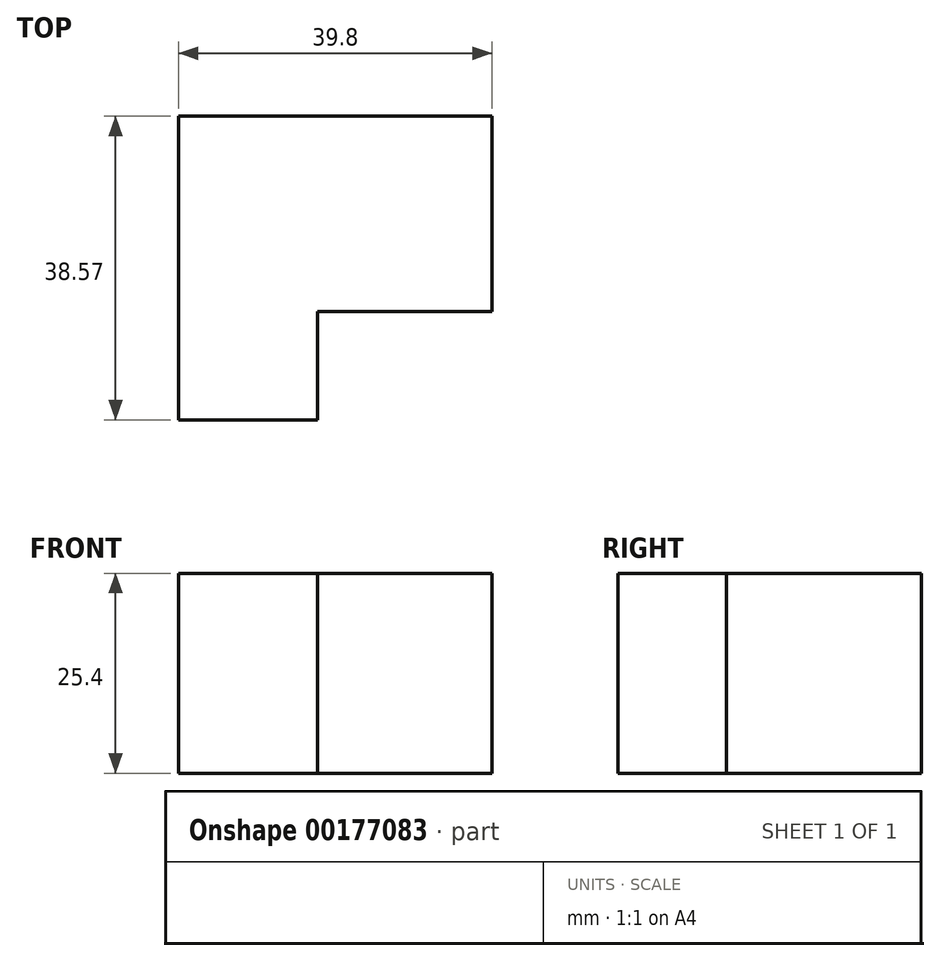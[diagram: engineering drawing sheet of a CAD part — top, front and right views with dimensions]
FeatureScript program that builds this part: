
annotation { "Feature Type Name" : "Feature", "Feature Type Description" : "" }
export const myFeature = defineFeature(function(context is Context, id is Id, definition is map)
    precondition{}
    {
        {
            var Q0;
            Q0=qCreatedBy(makeId("Top.planeOp"),FACE);
            var sketch = newSketch(context, id + "F0", { "sketchPlane" : qUnion([Q0])});
            skLineSegment(sketch, "E0.bottom", {"start": v(0, 0) * mm, "end": v(17.65, 0) * mm});
            skLineSegment(sketch, "E0.top", {"start": v(0, 24.33) * mm, "end": v(17.65, 24.33) * mm});
            skLineSegment(sketch, "E0.left", {"start": v(0, 0) * mm, "end": v(0, 24.33) * mm});
            skLineSegment(sketch, "E0.right", {"start": v(17.65, 0) * mm, "end": v(17.65, 24.33) * mm});
            skLineSegment(sketch, "E1.bottom", {"start": v(17.65, 24.33) * mm, "end": v(39.8, 24.33) * mm});
            skLineSegment(sketch, "E1.top", {"start": v(17.65, 13.77) * mm, "end": v(39.8, 13.77) * mm});
            skLineSegment(sketch, "E1.left", {"start": v(17.65, 24.33) * mm, "end": v(17.65, 13.77) * mm});
            skLineSegment(sketch, "E1.right", {"start": v(39.8, 24.33) * mm, "end": v(39.8, 13.77) * mm});
            skLineSegment(sketch, "E2.bottom", {"start": v(0, 24.33) * mm, "end": v(27.53, 24.33) * mm});
            skLineSegment(sketch, "E2.top", {"start": v(0, 38.57) * mm, "end": v(27.53, 38.57) * mm});
            skLineSegment(sketch, "E2.left", {"start": v(0, 24.33) * mm, "end": v(0, 38.57) * mm});
            skLineSegment(sketch, "E2.right", {"start": v(27.53, 24.33) * mm, "end": v(27.53, 38.57) * mm});
            skSolve(sketch);
        }
        {
            var Q0;
            Q0=makeQuery(id+"F0.imprint","IMPRINT",FACE,{"disambiguationData":[TD([[makeQuery(id+"F0.imprint","IMPRINT",EDGE,{"derivedFrom":sQuery(id+"F0.wireOp",EDGE,"E2.top")}),-1.0]])]});
            var Q1;
            Q1=makeQuery(id+"F0.imprint","IMPRINT",FACE,{"disambiguationData":[TD([[makeQuery(id+"F0.imprint","IMPRINT",EDGE,{"derivedFrom":sQuery(id+"F0.wireOp",EDGE,"E0.bottom")}),1.0]])]});
            var Q2;
            {var subQ1=sQuery(id+"F0.wireOp",EDGE,"E1.bottom");Q2=makeQuery(id+"F0.imprint","IMPRINT",FACE,{"disambiguationData":[TD([[makeQuery(id+"F0.imprint","IMPRINT",EDGE,{"derivedFrom":subQ1}),-1.0]])]});}
            extrude(context, id + "F1", {"entities" : qUnion([Q0, Q1, Q2]), "depth" : 25.4 * mm});
        }
        {
            var Q0;
            Q0=makeQuery(id+"F1.opExtrude","SWEPT_FACE",FACE,{"disambiguationData":[OSD([sQuery(id+"F0.wireOp",EDGE,"E2.right")])]});
            var Q1;
            Q1=makeQuery(id+"F1.opExtrude","SWEPT_FACE",FACE,{"disambiguationData":[OSD([sQuery(id+"F0.wireOp",EDGE,"E1.right")])]});
            var Q2;
            Q2=makeQuery(id+"F1.opExtrude","SWEPT_FACE",FACE,{"disambiguationData":[OSD([sQuery(id+"F0.wireOp",EDGE,"E1.right")])]});
            var Q3;
            Q3=makeQuery(id+"F1.opExtrude","SWEPT_BODY",BODY,{"disambiguationData":[OSD([sQuery(id+"F0.wireOp",EDGE,"E0.bottom"),sQuery(id+"F0.wireOp",EDGE,"E0.left"),sQuery(id+"F0.wireOp",EDGE,"E0.right"),sQuery(id+"F0.wireOp",EDGE,"E1.bottom"),sQuery(id+"F0.wireOp",EDGE,"E1.top"),sQuery(id+"F0.wireOp",EDGE,"E1.right"),sQuery(id+"F0.wireOp",EDGE,"E2.top"),sQuery(id+"F0.wireOp",EDGE,"E2.left"),sQuery(id+"F0.wireOp",EDGE,"E2.right")])]});
            extrude(context, id + "F2", {"entities" : qUnion([Q0]), "operationType" : NewBodyOperationType.ADD, "endBound" : BoundingType.UP_TO_SURFACE, "endBoundEntityFace" : qUnion([Q1]), "depth" : 25.4 * mm});
        }
    });
